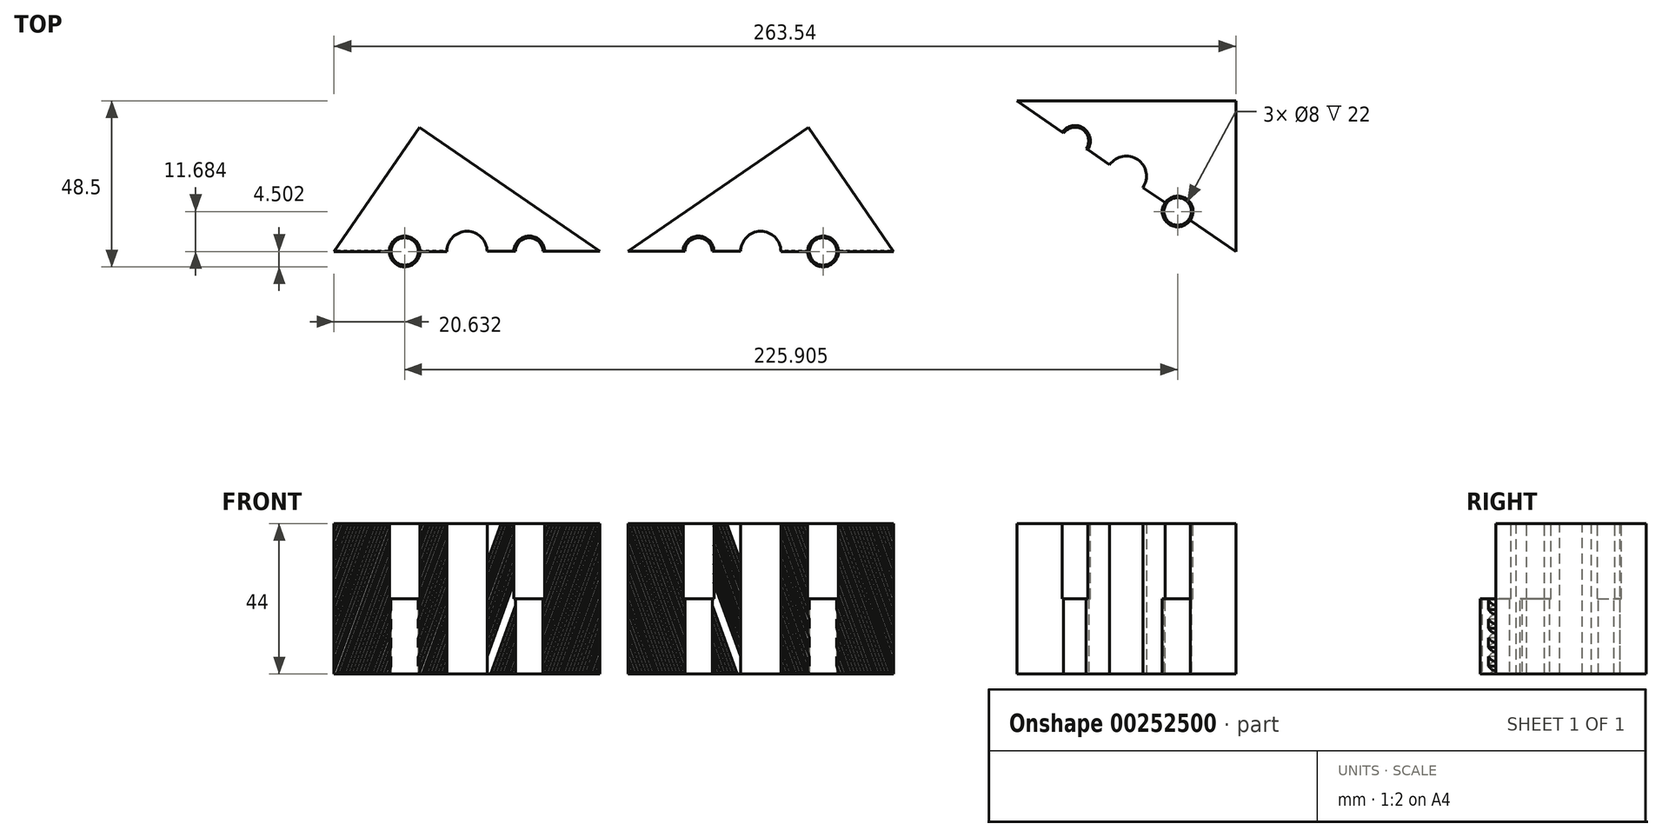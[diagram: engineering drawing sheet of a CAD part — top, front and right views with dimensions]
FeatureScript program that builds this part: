
annotation { "Feature Type Name" : "Feature", "Feature Type Description" : "" }
export const myFeature = defineFeature(function(context is Context, id is Id, definition is map)
    precondition{}
    {
        {
            var Q0;
            Q0=qCreatedBy(makeId("Top.planeOp"),FACE);
            var sketch = newSketch(context, id + "F0", { "sketchPlane" : qUnion([Q0])});
            skLineSegment(sketch, "E0.bottom", {"start": v(17.77, 54.78) * mm, "end": v(81.77, 54.78) * mm});
            skLineSegment(sketch, "E0.top", {"start": v(17.77, 10.78) * mm, "end": v(81.77, 10.78) * mm});
            skLineSegment(sketch, "E0.left", {"start": v(17.77, 54.78) * mm, "end": v(17.77, 10.78) * mm});
            skLineSegment(sketch, "E0.right", {"start": v(81.77, 54.78) * mm, "end": v(81.77, 10.78) * mm});
            skCircle(sketch, "E1", {"center": v(49.77, 32.78) * mm, "radius": 5.88 * mm});
            skPoint(sketch, "E1.centerSnap0", {"position": v(49.77, 54.78) * mm});
            skPoint(sketch, "E1.centerSnap1", {"position": v(17.77, 32.78) * mm});
            skCircle(sketch, "E2", {"center": v(34.77, 43.1) * mm, "radius": 4.5 * mm});
            skCircle(sketch, "E3", {"center": v(64.77, 22.47) * mm, "radius": 4.5 * mm});
            skLineSegment(sketch, "E4", {"start": v(34.77, -31.73) * mm, "end": v(64.77, -31.73) * mm, "construction": true});
            skPoint(sketch, "E5", {"position": v(49.77, -31.73) * mm});
            skLineSegment(sketch, "E6", {"start": v(17.77, 54.78) * mm, "end": v(81.77, 10.78) * mm, "construction": true});
            skCircle(sketch, "E7", {"center": v(34.77, 43.1) * mm, "radius": 4 * mm});
            skCircle(sketch, "E8", {"center": v(64.77, 22.47) * mm, "radius": 4 * mm});
            skSolve(sketch);
        }
        {
            var Q0;
            Q0=makeQuery(id+"F0.imprint","IMPRINT",FACE,{"disambiguationData":[TD([[makeQuery(id+"F0.imprint","IMPRINT",EDGE,{"derivedFrom":sQuery(id+"F0.wireOp",EDGE,"E0.bottom")}),-1.0]])]});
            var Q1;
            Q1=makeQuery(id+"F0.imprint","IMPRINT",FACE,{"disambiguationData":[TD([[makeQuery(id+"F0.imprint","IMPRINT",EDGE,{"derivedFrom":sQuery(id+"F0.wireOp",EDGE,"E3")}),1.0]])]});
            var Q2;
            Q2=makeQuery(id+"F0.imprint","IMPRINT",FACE,{"disambiguationData":[TD([[makeQuery(id+"F0.imprint","IMPRINT",EDGE,{"derivedFrom":sQuery(id+"F0.wireOp",EDGE,"E2")}),1.0]])]});
            extrude(context, id + "F1", {"entities" : qUnion([Q0, Q1, Q2]), "depth" : 44 * mm});
        }
        {
            var Q0;
            Q0=makeQuery(id+"F0.imprint","IMPRINT",FACE,{"disambiguationData":[TD([[makeQuery(id+"F0.imprint","IMPRINT",EDGE,{"derivedFrom":sQuery(id+"F0.wireOp",EDGE,"E1")}),1.0]])]});
            extrude(context, id + "F2", {"entities" : qUnion([Q0]), "operationType" : NewBodyOperationType.REMOVE, "depth" : 25 * mm});
        }
        {
            var Q0;
            Q0=makeQuery(id+"F1.opExtrude","CAP_FACE",FACE,{"disambiguationData":[OSD([sQuery(id+"F0.wireOp",EDGE,"E0.bottom"),sQuery(id+"F0.wireOp",EDGE,"E0.top"),sQuery(id+"F0.wireOp",EDGE,"E0.left"),sQuery(id+"F0.wireOp",EDGE,"E0.right"),sQuery(id+"F0.wireOp",EDGE,"E1"),sQuery(id+"F0.wireOp",EDGE,"E7"),sQuery(id+"F0.wireOp",EDGE,"E8")])],"isStart":false});
            var sketch = newSketch(context, id + "F3", { "sketchPlane" : qUnion([Q0])});
            skCircle(sketch, "E9", {"center": v(34.77, 43.1) * mm, "radius": 4 * mm});
            skCircle(sketch, "E10", {"center": v(64.77, 22.47) * mm, "radius": 4 * mm});
            skCircle(sketch, "E11", {"center": v(64.77, 22.47) * mm, "radius": 4.5 * mm});
            skCircle(sketch, "E12", {"center": v(34.77, 43.1) * mm, "radius": 4.5 * mm});
            skSolve(sketch);
        }
        {
            var Q0;
            Q0=makeQuery(id+"F3.imprint","IMPRINT",FACE,{"disambiguationData":[TD([[makeQuery(id+"F3.imprint","IMPRINT",EDGE,{"derivedFrom":sQuery(id+"F3.wireOp",EDGE,"E10")}),-1.0]])]});
            var Q1;
            Q1=makeQuery(id+"F3.imprint","IMPRINT",FACE,{"disambiguationData":[TD([[makeQuery(id+"F3.imprint","IMPRINT",EDGE,{"derivedFrom":sQuery(id+"F3.wireOp",EDGE,"E9")}),-1.0]])]});
            extrude(context, id + "F4", {"entities" : qUnion([Q0, Q1]), "operationType" : NewBodyOperationType.REMOVE, "oppositeDirection" : true, "depth" : 22 * mm});
        }
        {
            var Q0;
            Q0=makeQuery(id+"F1.opExtrude","CAP_FACE",FACE,{"disambiguationData":[OSD([sQuery(id+"F0.wireOp",EDGE,"E0.bottom"),sQuery(id+"F0.wireOp",EDGE,"E0.top"),sQuery(id+"F0.wireOp",EDGE,"E0.left"),sQuery(id+"F0.wireOp",EDGE,"E0.right"),sQuery(id+"F0.wireOp",EDGE,"E1"),sQuery(id+"F0.wireOp",EDGE,"E7"),sQuery(id+"F0.wireOp",EDGE,"E8")])],"isStart":false});
            var sketch = newSketch(context, id + "F5", { "sketchPlane" : qUnion([Q0])});
            skLineSegment(sketch, "E13", {"start": v(17.77, 54.78) * mm, "end": v(17.77, 10.78) * mm});
            skLineSegment(sketch, "E14", {"start": v(17.77, 10.78) * mm, "end": v(81.77, 10.78) * mm});
            skLineSegment(sketch, "E15", {"start": v(81.77, 10.78) * mm, "end": v(17.77, 54.78) * mm});
            skArc(sketch, "E16", {"start": v(31.06, 45.64) * mm, "mid": v(32.22, 39.38) * mm, "end": v(38.48, 40.54) * mm});
            skArc(sketch, "E17", {"start": v(31.47, 45.36) * mm, "mid": v(32.5, 39.8) * mm, "end": v(38.06, 40.83) * mm});
            skSolve(sketch);
        }
        {
            var Q0;
            {var subQ10=sQuery(id+"F5.wireOp",EDGE,"E13");Q0=makeQuery(id+"F5.imprint","IMPRINT",FACE,{"disambiguationData":[TD([[makeQuery(id+"F5.imprint","IMPRINT",EDGE,{"derivedFrom":subQ10}),1.0]])]});}
            var Q1;
            {var subQ0=sQuery(id+"F5.wireOp",EDGE,"E16");Q1=makeQuery(id+"F5.imprint","IMPRINT",FACE,{"disambiguationData":[TD([[makeQuery(id+"F5.imprint","IMPRINT",EDGE,{"derivedFrom":subQ0}),1.0]])]});}
            var Q2;
            {var subQ0=sQuery(id+"F5.wireOp",EDGE,"E15");var subQ1=makeQuery(id+"F4.boolean.opBoolean","COPY",EDGE,{"derivedFrom":makeQuery(id+"F4.opExtrude","CAP_EDGE",EDGE,{"disambiguationData":[OSD([sQuery(id+"F3.wireOp",EDGE,"E11")])],"isStart":true})});var subQ2=makeQuery(id+"F5.imprint","INTERSECT",VERTEX,{"disambiguationData":[OD(0.0)],"derivedFrom":[subQ1,subQ0]});Q2=makeQuery(id+"F5.imprint","IMPRINT",FACE,{"disambiguationData":[TD([[makeQuery(id+"F5.imprint","IMPRINT",EDGE,{"disambiguationData":[TD([[subQ2,-1.0]])],"derivedFrom":subQ0}),1.0]])]});}
            extrude(context, id + "F6", {"entities" : qUnion([Q0, Q1, Q2]), "operationType" : NewBodyOperationType.REMOVE, "oppositeDirection" : true, "depth" : 100 * mm});
        }
        {
            var Q0;
            Q0=makeQuery(id+"F1.opExtrude","SWEPT_BODY",BODY,{"disambiguationData":[OSD([sQuery(id+"F0.wireOp",EDGE,"E0.bottom"),sQuery(id+"F0.wireOp",EDGE,"E0.top"),sQuery(id+"F0.wireOp",EDGE,"E0.left"),sQuery(id+"F0.wireOp",EDGE,"E0.right"),sQuery(id+"F0.wireOp",EDGE,"E1"),sQuery(id+"F0.wireOp",EDGE,"E7"),sQuery(id+"F0.wireOp",EDGE,"E8")])]});
            transform(context, id + "F7", {"entities" : qUnion([Q0]), "transformType" : TransformType.TRANSLATION_3D, "dx" : 100 * mm, "dy" : 0 * mm, "dz" : 0 * mm, "makeCopy" : true});
        }
        {
            var Q0;
            Q0=makeQuery(id+"F1.opExtrude","SWEPT_BODY",BODY,{"disambiguationData":[OSD([sQuery(id+"F0.wireOp",EDGE,"E0.bottom"),sQuery(id+"F0.wireOp",EDGE,"E0.top"),sQuery(id+"F0.wireOp",EDGE,"E0.left"),sQuery(id+"F0.wireOp",EDGE,"E0.right"),sQuery(id+"F0.wireOp",EDGE,"E1"),sQuery(id+"F0.wireOp",EDGE,"E7"),sQuery(id+"F0.wireOp",EDGE,"E8")])]});
            var Q1;
            {var subQ0=sQuery(id+"F0.wireOp",EDGE,"E0.right");Q1=makeQuery(id+"F6.boolean.opBoolean","MERGE",EDGE,{"derivedFrom":[makeQuery(id+"F1.opExtrude","SWEPT_EDGE",EDGE,{"disambiguationData":[OSD([sQuery(id+"F0.wireOp",EDGE,"E0.top"),subQ0])]}),makeQuery(id+"F6.opExtrude","SWEPT_EDGE",EDGE,{"disambiguationData":[OSD([subQ0,sQuery(id+"F5.wireOp",EDGE,"E14"),sQuery(id+"F5.wireOp",EDGE,"E15")])]})]});}
            transform(context, id + "F8", {"entities" : qUnion([Q0]), "transformType" : TransformType.ROTATION, "transformAxis" : qUnion([Q1]), "angle" : 34.5 * degree, "oppositeDirection" : true, "makeCopy" : false});
        }
        {
            var Q0;
            Q0=qCreatedBy(makeId("Front.planeOp"),FACE);
            var sketch = newSketch(context, id + "F9", { "sketchPlane" : qUnion([Q0])});
            skLineSegment(sketch, "E18.bottom", {"start": v(-39.61, 0) * mm, "end": v(60.39, 0) * mm, "construction": true});
            skLineSegment(sketch, "E18.top", {"start": v(-39.61, 100) * mm, "end": v(60.39, 100) * mm, "construction": true});
            skLineSegment(sketch, "E18.left", {"start": v(-39.61, 0) * mm, "end": v(-39.61, 100) * mm, "construction": true});
            skLineSegment(sketch, "E18.right", {"start": v(60.39, 0) * mm, "end": v(60.39, 100) * mm, "construction": true});
            skLineSegment(sketch, "E19", {"start": v(-6.03, 0) * mm, "end": v(-39.61, 92.27) * mm});
            skLineSegment(sketch, "E20.1.0.0", {"start": v(-5.03, 0) * mm, "end": v(-38.61, 92.27) * mm});
            skLineSegment(sketch, "E20.2.0.0", {"start": v(-4.03, 0) * mm, "end": v(-37.61, 92.27) * mm});
            skLineSegment(sketch, "E20.3.0.0", {"start": v(-3.03, 0) * mm, "end": v(-36.61, 92.27) * mm});
            skLineSegment(sketch, "E20.4.0.0", {"start": v(-2.03, 0) * mm, "end": v(-35.61, 92.27) * mm});
            skLineSegment(sketch, "E20.5.0.0", {"start": v(-1.03, 0) * mm, "end": v(-34.61, 92.27) * mm});
            skLineSegment(sketch, "E20.6.0.0", {"start": v(-0.03, 0) * mm, "end": v(-33.61, 92.27) * mm});
            skLineSegment(sketch, "E20.7.0.0", {"start": v(0.97, 0) * mm, "end": v(-32.61, 92.27) * mm});
            skLineSegment(sketch, "E20.8.0.0", {"start": v(1.97, 0) * mm, "end": v(-31.61, 92.27) * mm});
            skLineSegment(sketch, "E20.9.0.0", {"start": v(2.97, 0) * mm, "end": v(-30.61, 92.27) * mm});
            skLineSegment(sketch, "E20.10.0.0", {"start": v(3.97, 0) * mm, "end": v(-29.61, 92.27) * mm});
            skLineSegment(sketch, "E20.11.0.0", {"start": v(4.97, 0) * mm, "end": v(-28.61, 92.27) * mm});
            skLineSegment(sketch, "E20.12.0.0", {"start": v(5.97, 0) * mm, "end": v(-27.61, 92.27) * mm});
            skLineSegment(sketch, "E20.13.0.0", {"start": v(6.97, 0) * mm, "end": v(-26.61, 92.27) * mm});
            skLineSegment(sketch, "E20.14.0.0", {"start": v(7.97, 0) * mm, "end": v(-25.61, 92.27) * mm});
            skLineSegment(sketch, "E20.15.0.0", {"start": v(8.97, 0) * mm, "end": v(-24.61, 92.27) * mm});
            skLineSegment(sketch, "E20.16.0.0", {"start": v(9.97, 0) * mm, "end": v(-23.61, 92.27) * mm});
            skLineSegment(sketch, "E20.17.0.0", {"start": v(10.97, 0) * mm, "end": v(-22.61, 92.27) * mm});
            skLineSegment(sketch, "E20.18.0.0", {"start": v(11.97, 0) * mm, "end": v(-21.61, 92.27) * mm});
            skLineSegment(sketch, "E20.19.0.0", {"start": v(12.97, 0) * mm, "end": v(-20.61, 92.27) * mm});
            skLineSegment(sketch, "E20.20.0.0", {"start": v(13.97, 0) * mm, "end": v(-19.61, 92.27) * mm});
            skLineSegment(sketch, "E20.21.0.0", {"start": v(14.97, 0) * mm, "end": v(-18.61, 92.27) * mm});
            skLineSegment(sketch, "E20.22.0.0", {"start": v(15.97, 0) * mm, "end": v(-17.61, 92.27) * mm});
            skLineSegment(sketch, "E20.23.0.0", {"start": v(16.97, 0) * mm, "end": v(-16.61, 92.27) * mm});
            skLineSegment(sketch, "E20.24.0.0", {"start": v(17.97, 0) * mm, "end": v(-15.61, 92.27) * mm});
            skLineSegment(sketch, "E20.25.0.0", {"start": v(18.97, 0) * mm, "end": v(-14.61, 92.27) * mm});
            skLineSegment(sketch, "E20.26.0.0", {"start": v(19.97, 0) * mm, "end": v(-13.61, 92.27) * mm});
            skLineSegment(sketch, "E20.27.0.0", {"start": v(20.97, 0) * mm, "end": v(-12.61, 92.27) * mm});
            skLineSegment(sketch, "E20.28.0.0", {"start": v(21.97, 0) * mm, "end": v(-11.61, 92.27) * mm});
            skLineSegment(sketch, "E20.29.0.0", {"start": v(22.97, 0) * mm, "end": v(-10.61, 92.27) * mm});
            skLineSegment(sketch, "E20.30.0.0", {"start": v(23.97, 0) * mm, "end": v(-9.61, 92.27) * mm});
            skLineSegment(sketch, "E20.31.0.0", {"start": v(24.97, 0) * mm, "end": v(-8.61, 92.27) * mm});
            skLineSegment(sketch, "E20.32.0.0", {"start": v(25.97, 0) * mm, "end": v(-7.61, 92.27) * mm});
            skLineSegment(sketch, "E20.33.0.0", {"start": v(26.97, 0) * mm, "end": v(-6.61, 92.27) * mm});
            skLineSegment(sketch, "E20.34.0.0", {"start": v(27.97, 0) * mm, "end": v(-5.61, 92.27) * mm});
            skLineSegment(sketch, "E20.35.0.0", {"start": v(28.97, 0) * mm, "end": v(-4.61, 92.27) * mm});
            skLineSegment(sketch, "E20.36.0.0", {"start": v(29.97, 0) * mm, "end": v(-3.61, 92.27) * mm});
            skLineSegment(sketch, "E20.37.0.0", {"start": v(30.97, 0) * mm, "end": v(-2.61, 92.27) * mm});
            skLineSegment(sketch, "E20.38.0.0", {"start": v(31.97, 0) * mm, "end": v(-1.61, 92.27) * mm});
            skLineSegment(sketch, "E20.39.0.0", {"start": v(32.97, 0) * mm, "end": v(-0.61, 92.27) * mm});
            skLineSegment(sketch, "E20.40.0.0", {"start": v(33.97, 0) * mm, "end": v(0.39, 92.27) * mm});
            skLineSegment(sketch, "E20.41.0.0", {"start": v(34.97, 0) * mm, "end": v(1.39, 92.27) * mm});
            skLineSegment(sketch, "E20.42.0.0", {"start": v(35.97, 0) * mm, "end": v(2.39, 92.27) * mm});
            skLineSegment(sketch, "E20.43.0.0", {"start": v(36.97, 0) * mm, "end": v(3.39, 92.27) * mm});
            skLineSegment(sketch, "E20.44.0.0", {"start": v(37.97, 0) * mm, "end": v(4.39, 92.27) * mm});
            skLineSegment(sketch, "E20.45.0.0", {"start": v(38.97, 0) * mm, "end": v(5.39, 92.27) * mm});
            skLineSegment(sketch, "E20.46.0.0", {"start": v(39.97, 0) * mm, "end": v(6.39, 92.27) * mm});
            skLineSegment(sketch, "E20.47.0.0", {"start": v(40.97, 0) * mm, "end": v(7.39, 92.27) * mm});
            skLineSegment(sketch, "E20.48.0.0", {"start": v(41.97, 0) * mm, "end": v(8.39, 92.27) * mm});
            skLineSegment(sketch, "E20.49.0.0", {"start": v(42.97, 0) * mm, "end": v(9.39, 92.27) * mm});
            skLineSegment(sketch, "E20.50.0.0", {"start": v(43.97, 0) * mm, "end": v(10.39, 92.27) * mm});
            skLineSegment(sketch, "E20.51.0.0", {"start": v(44.97, 0) * mm, "end": v(11.39, 92.27) * mm});
            skLineSegment(sketch, "E20.52.0.0", {"start": v(45.97, 0) * mm, "end": v(12.39, 92.27) * mm});
            skLineSegment(sketch, "E20.53.0.0", {"start": v(46.97, 0) * mm, "end": v(13.39, 92.27) * mm});
            skLineSegment(sketch, "E20.54.0.0", {"start": v(47.97, 0) * mm, "end": v(14.39, 92.27) * mm});
            skLineSegment(sketch, "E20.55.0.0", {"start": v(48.97, 0) * mm, "end": v(15.39, 92.27) * mm});
            skLineSegment(sketch, "E20.56.0.0", {"start": v(49.97, 0) * mm, "end": v(16.39, 92.27) * mm});
            skLineSegment(sketch, "E20.57.0.0", {"start": v(50.97, 0) * mm, "end": v(17.39, 92.27) * mm});
            skLineSegment(sketch, "E20.58.0.0", {"start": v(51.97, 0) * mm, "end": v(18.39, 92.27) * mm});
            skLineSegment(sketch, "E20.59.0.0", {"start": v(52.97, 0) * mm, "end": v(19.39, 92.27) * mm});
            skLineSegment(sketch, "E20.60.0.0", {"start": v(53.97, 0) * mm, "end": v(20.39, 92.27) * mm});
            skLineSegment(sketch, "E20.61.0.0", {"start": v(54.97, 0) * mm, "end": v(21.39, 92.27) * mm});
            skLineSegment(sketch, "E20.62.0.0", {"start": v(55.97, 0) * mm, "end": v(22.39, 92.27) * mm});
            skLineSegment(sketch, "E20.63.0.0", {"start": v(56.97, 0) * mm, "end": v(23.39, 92.27) * mm});
            skLineSegment(sketch, "E20.64.0.0", {"start": v(57.97, 0) * mm, "end": v(24.39, 92.27) * mm});
            skLineSegment(sketch, "E20.65.0.0", {"start": v(58.97, 0) * mm, "end": v(25.39, 92.27) * mm});
            skLineSegment(sketch, "E20.66.0.0", {"start": v(59.97, 0) * mm, "end": v(26.39, 92.27) * mm});
            skLineSegment(sketch, "E20.67.0.0", {"start": v(60.97, 0) * mm, "end": v(27.39, 92.27) * mm});
            skLineSegment(sketch, "E20.68.0.0", {"start": v(61.97, 0) * mm, "end": v(28.39, 92.27) * mm});
            skLineSegment(sketch, "E20.69.0.0", {"start": v(62.97, 0) * mm, "end": v(29.39, 92.27) * mm});
            skLineSegment(sketch, "E20.70.0.0", {"start": v(63.97, 0) * mm, "end": v(30.39, 92.27) * mm});
            skLineSegment(sketch, "E20.71.0.0", {"start": v(64.97, 0) * mm, "end": v(31.39, 92.27) * mm});
            skLineSegment(sketch, "E20.72.0.0", {"start": v(65.97, 0) * mm, "end": v(32.39, 92.27) * mm});
            skLineSegment(sketch, "E20.73.0.0", {"start": v(66.97, 0) * mm, "end": v(33.39, 92.27) * mm});
            skLineSegment(sketch, "E20.74.0.0", {"start": v(67.97, 0) * mm, "end": v(34.39, 92.27) * mm});
            skLineSegment(sketch, "E20.75.0.0", {"start": v(68.97, 0) * mm, "end": v(35.39, 92.27) * mm});
            skLineSegment(sketch, "E20.76.0.0", {"start": v(69.97, 0) * mm, "end": v(36.39, 92.27) * mm});
            skLineSegment(sketch, "E20.77.0.0", {"start": v(70.97, 0) * mm, "end": v(37.39, 92.27) * mm});
            skLineSegment(sketch, "E20.78.0.0", {"start": v(71.97, 0) * mm, "end": v(38.39, 92.27) * mm});
            skLineSegment(sketch, "E20.79.0.0", {"start": v(72.97, 0) * mm, "end": v(39.39, 92.27) * mm});
            skLineSegment(sketch, "E20.80.0.0", {"start": v(73.97, 0) * mm, "end": v(40.39, 92.27) * mm});
            skLineSegment(sketch, "E20.81.0.0", {"start": v(74.97, 0) * mm, "end": v(41.39, 92.27) * mm});
            skLineSegment(sketch, "E20.82.0.0", {"start": v(75.97, 0) * mm, "end": v(42.39, 92.27) * mm});
            skLineSegment(sketch, "E20.83.0.0", {"start": v(76.97, 0) * mm, "end": v(43.39, 92.27) * mm});
            skLineSegment(sketch, "E20.84.0.0", {"start": v(77.97, 0) * mm, "end": v(44.39, 92.27) * mm});
            skLineSegment(sketch, "E20.85.0.0", {"start": v(78.97, 0) * mm, "end": v(45.39, 92.27) * mm});
            skLineSegment(sketch, "E20.86.0.0", {"start": v(79.97, 0) * mm, "end": v(46.39, 92.27) * mm});
            skLineSegment(sketch, "E20.87.0.0", {"start": v(80.97, 0) * mm, "end": v(47.39, 92.27) * mm});
            skLineSegment(sketch, "E20.88.0.0", {"start": v(81.97, 0) * mm, "end": v(48.39, 92.27) * mm});
            skLineSegment(sketch, "E20.89.0.0", {"start": v(82.97, 0) * mm, "end": v(49.39, 92.27) * mm});
            skLineSegment(sketch, "E20.90.0.0", {"start": v(83.97, 0) * mm, "end": v(50.39, 92.27) * mm});
            skLineSegment(sketch, "E20.91.0.0", {"start": v(84.97, 0) * mm, "end": v(51.39, 92.27) * mm});
            skLineSegment(sketch, "E20.92.0.0", {"start": v(85.97, 0) * mm, "end": v(52.39, 92.27) * mm});
            skLineSegment(sketch, "E20.93.0.0", {"start": v(86.97, 0) * mm, "end": v(53.39, 92.27) * mm});
            skLineSegment(sketch, "E20.94.0.0", {"start": v(87.97, 0) * mm, "end": v(54.39, 92.27) * mm});
            skLineSegment(sketch, "E20.95.0.0", {"start": v(88.97, 0) * mm, "end": v(55.39, 92.27) * mm});
            skLineSegment(sketch, "E20.96.0.0", {"start": v(89.97, 0) * mm, "end": v(56.39, 92.27) * mm});
            skLineSegment(sketch, "E20.97.0.0", {"start": v(90.97, 0) * mm, "end": v(57.39, 92.27) * mm});
            skLineSegment(sketch, "E20.98.0.0", {"start": v(91.97, 0) * mm, "end": v(58.39, 92.27) * mm});
            skLineSegment(sketch, "E20.99.0.0", {"start": v(92.97, 0) * mm, "end": v(59.39, 92.27) * mm});
            skLineSegment(sketch, "E20.direction1", {"start": v(-6.03, 0) * mm, "end": v(-5.03, 0) * mm, "construction": true});
            skLineSegment(sketch, "E21.top", {"start": v(37.77, 0) * mm, "end": v(44.67, 0) * mm});
            skLineSegment(sketch, "E22", {"start": v(48.67, 0) * mm, "end": v(56.77, 0) * mm});
            skLineSegment(sketch, "E23.MirrorCS", {"start": v(139.15, 0) * mm, "end": v(39.15, 0) * mm, "construction": true});
            skLineSegment(sketch, "E24.bottom", {"start": v(20.23, 44) * mm, "end": v(29.23, 44) * mm});
            skLineSegment(sketch, "E24.top", {"start": v(20.23, 22) * mm, "end": v(29.23, 22) * mm});
            skLineSegment(sketch, "E24.left", {"start": v(20.23, 44) * mm, "end": v(20.23, 22) * mm});
            skLineSegment(sketch, "E24.right", {"start": v(29.23, 44) * mm, "end": v(29.23, 22) * mm});
            skLineSegment(sketch, "E25.bottom", {"start": v(20.73, 22) * mm, "end": v(28.73, 22) * mm});
            skLineSegment(sketch, "E25.top", {"start": v(20.73, 0) * mm, "end": v(28.73, 0) * mm});
            skLineSegment(sketch, "E25.left", {"start": v(20.73, 22) * mm, "end": v(20.73, 0) * mm});
            skLineSegment(sketch, "E25.right", {"start": v(28.73, 22) * mm, "end": v(28.73, 0) * mm});
            skLineSegment(sketch, "E26", {"start": v(4.1, -46.77) * mm, "end": v(81.77, -46.77) * mm, "construction": true});
            skPoint(sketch, "E27", {"position": v(4.1, 1.38) * mm});
            skPoint(sketch, "E28", {"position": v(42.93, -46.77) * mm});
            skLineSegment(sketch, "E29", {"start": v(20.73, -2) * mm, "end": v(28.73, -2) * mm, "construction": true});
            skLineSegment(sketch, "E30.bottom", {"start": v(56.64, 44) * mm, "end": v(65.64, 44) * mm});
            skLineSegment(sketch, "E30.top", {"start": v(56.64, 22) * mm, "end": v(65.64, 22) * mm});
            skLineSegment(sketch, "E30.left", {"start": v(56.64, 44) * mm, "end": v(56.64, 22) * mm});
            skLineSegment(sketch, "E30.right", {"start": v(65.64, 44) * mm, "end": v(65.64, 22) * mm});
            skLineSegment(sketch, "E31.bottom", {"start": v(57.14, 22) * mm, "end": v(65.14, 22) * mm});
            skLineSegment(sketch, "E31.top", {"start": v(57.14, 0) * mm, "end": v(65.14, 0) * mm});
            skLineSegment(sketch, "E31.left", {"start": v(57.14, 22) * mm, "end": v(57.14, 0) * mm});
            skLineSegment(sketch, "E31.right", {"start": v(65.14, 22) * mm, "end": v(65.14, 0) * mm});
            skLineSegment(sketch, "E32.bottom", {"start": v(4.1, 44) * mm, "end": v(20.23, 44) * mm});
            skLineSegment(sketch, "E32.left", {"start": v(4.1, 44) * mm, "end": v(4.1, 22) * mm});
            skLineSegment(sketch, "E33.top", {"start": v(4.1, 0) * mm, "end": v(20.73, 0) * mm});
            skLineSegment(sketch, "E33.left", {"start": v(4.1, 22) * mm, "end": v(4.1, 0) * mm});
            skLineSegment(sketch, "E34.trimOffspring", {"start": v(20.23, 22) * mm, "end": v(20.73, 22) * mm});
            skLineSegment(sketch, "E35.bottom", {"start": v(29.23, 44) * mm, "end": v(37.06, 44) * mm});
            skLineSegment(sketch, "E35.right", {"start": v(37.06, 44) * mm, "end": v(37.06, 22) * mm});
            skLineSegment(sketch, "E36.bottom", {"start": v(28.73, 22) * mm, "end": v(28.97, 22) * mm});
            skLineSegment(sketch, "E36.top", {"start": v(28.73, 0) * mm, "end": v(37.06, 0) * mm});
            skLineSegment(sketch, "E36.right", {"start": v(37.06, 22) * mm, "end": v(37.06, 0) * mm});
            skLineSegment(sketch, "E37.trimOffspring", {"start": v(36.97, 22) * mm, "end": v(37.06, 22) * mm});
            skLineSegment(sketch, "E38.top", {"start": v(57.14, 0) * mm, "end": v(48.8, 0) * mm});
            skLineSegment(sketch, "E38.right", {"start": v(48.8, 22) * mm, "end": v(48.8, 0) * mm});
            skLineSegment(sketch, "E39.top", {"start": v(56.64, 44) * mm, "end": v(48.8, 44) * mm});
            skLineSegment(sketch, "E39.left", {"start": v(56.64, 22) * mm, "end": v(56.64, 44) * mm});
            skLineSegment(sketch, "E39.right", {"start": v(48.8, 22) * mm, "end": v(48.8, 44) * mm});
            skLineSegment(sketch, "E40.1.0.0", {"start": v(93.97, 0) * mm, "end": v(60.39, 92.27) * mm});
            skLineSegment(sketch, "E40.2.0.0", {"start": v(94.97, 0) * mm, "end": v(61.39, 92.27) * mm});
            skLineSegment(sketch, "E40.3.0.0", {"start": v(95.97, 0) * mm, "end": v(62.39, 92.27) * mm});
            skLineSegment(sketch, "E40.4.0.0", {"start": v(96.97, 0) * mm, "end": v(63.39, 92.27) * mm});
            skLineSegment(sketch, "E40.5.0.0", {"start": v(97.97, 0) * mm, "end": v(64.39, 92.27) * mm});
            skLineSegment(sketch, "E40.6.0.0", {"start": v(98.97, 0) * mm, "end": v(65.39, 92.27) * mm});
            skLineSegment(sketch, "E40.7.0.0", {"start": v(99.97, 0) * mm, "end": v(66.39, 92.27) * mm});
            skLineSegment(sketch, "E40.8.0.0", {"start": v(100.97, 0) * mm, "end": v(67.39, 92.27) * mm});
            skLineSegment(sketch, "E40.9.0.0", {"start": v(101.97, 0) * mm, "end": v(68.39, 92.27) * mm});
            skLineSegment(sketch, "E40.direction1", {"start": v(92.97, 0) * mm, "end": v(93.97, 0) * mm, "construction": true});
            skLineSegment(sketch, "E41.bottom", {"start": v(65.64, 44) * mm, "end": v(81.77, 44) * mm});
            skLineSegment(sketch, "E41.right", {"start": v(81.77, 44) * mm, "end": v(81.77, 22) * mm});
            skLineSegment(sketch, "E42.bottom", {"start": v(65.14, 0) * mm, "end": v(81.77, 0) * mm});
            skLineSegment(sketch, "E42.left", {"start": v(65.14, 0) * mm, "end": v(65.14, 22) * mm});
            skLineSegment(sketch, "E42.right", {"start": v(81.77, 0) * mm, "end": v(81.77, 22) * mm});
            skLineSegment(sketch, "E43", {"start": v(4.2, 0) * mm, "end": v(4.2, 44) * mm});
            skLineSegment(sketch, "E44", {"start": v(42.93, -44.84) * mm, "end": v(42.93, -27.61) * mm, "construction": true});
            skLineSegment(sketch, "E45.MirrorCS", {"start": v(81.67, 0) * mm, "end": v(81.67, 44) * mm});
            skSolve(sketch);
        }
        {
            var Q0;
            Q0=qCreatedBy(makeId("Top.planeOp"),FACE);
            var sketch = newSketch(context, id + "F10", { "sketchPlane" : qUnion([Q0])});
            skLineSegment(sketch, "E46", {"start": v(-18.8, 10.9) * mm, "end": v(-18.7, 10.9) * mm, "construction": true});
            skSolve(sketch);
        }
        {
            var Q0;
            {var subQ0=sQuery(id+"F9.wireOp",EDGE,"E33.top");var subQ1=sQuery(id+"F9.wireOp",EDGE,"E20.13.0.0");var subQ2=makeQuery(id+"F9.imprint","INTERSECT",VERTEX,{"derivedFrom":[subQ1,subQ0]});Q0=makeQuery(id+"F9.imprint","IMPRINT",FACE,{"disambiguationData":[TD([[makeQuery(id+"F9.imprint","IMPRINT",EDGE,{"disambiguationData":[TD([[subQ2,-1.0]])],"derivedFrom":subQ1}),-1.0]])]});}
            var Q1;
            {var subQ0=sQuery(id+"F9.wireOp",EDGE,"E33.top");var subQ1=sQuery(id+"F9.wireOp",EDGE,"E20.15.0.0");var subQ2=makeQuery(id+"F9.imprint","INTERSECT",VERTEX,{"derivedFrom":[subQ1,subQ0]});Q1=makeQuery(id+"F9.imprint","IMPRINT",FACE,{"disambiguationData":[TD([[makeQuery(id+"F9.imprint","IMPRINT",EDGE,{"disambiguationData":[TD([[subQ2,-1.0]])],"derivedFrom":subQ1}),-1.0]])]});}
            var Q2;
            {var subQ0=sQuery(id+"F9.wireOp",EDGE,"E33.top");var subQ1=sQuery(id+"F9.wireOp",EDGE,"E20.17.0.0");var subQ2=makeQuery(id+"F9.imprint","INTERSECT",VERTEX,{"derivedFrom":[subQ1,subQ0]});Q2=makeQuery(id+"F9.imprint","IMPRINT",FACE,{"disambiguationData":[TD([[makeQuery(id+"F9.imprint","IMPRINT",EDGE,{"disambiguationData":[TD([[subQ2,-1.0]])],"derivedFrom":subQ1}),-1.0]])]});}
            var Q3;
            {var subQ0=sQuery(id+"F9.wireOp",EDGE,"E33.top");var subQ1=sQuery(id+"F9.wireOp",EDGE,"E20.19.0.0");var subQ2=makeQuery(id+"F9.imprint","INTERSECT",VERTEX,{"derivedFrom":[subQ1,subQ0]});Q3=makeQuery(id+"F9.imprint","IMPRINT",FACE,{"disambiguationData":[TD([[makeQuery(id+"F9.imprint","IMPRINT",EDGE,{"disambiguationData":[TD([[subQ2,-1.0]])],"derivedFrom":subQ1}),-1.0]])]});}
            var Q4;
            {var subQ0=sQuery(id+"F9.wireOp",EDGE,"E33.top");var subQ1=sQuery(id+"F9.wireOp",EDGE,"E20.21.0.0");var subQ2=makeQuery(id+"F9.imprint","INTERSECT",VERTEX,{"derivedFrom":[subQ1,subQ0]});Q4=makeQuery(id+"F9.imprint","IMPRINT",FACE,{"disambiguationData":[TD([[makeQuery(id+"F9.imprint","IMPRINT",EDGE,{"disambiguationData":[TD([[subQ2,-1.0]])],"derivedFrom":subQ1}),-1.0]])]});}
            var Q5;
            {var subQ0=sQuery(id+"F9.wireOp",EDGE,"E33.top");var subQ1=sQuery(id+"F9.wireOp",EDGE,"E20.23.0.0");var subQ2=makeQuery(id+"F9.imprint","INTERSECT",VERTEX,{"derivedFrom":[subQ1,subQ0]});Q5=makeQuery(id+"F9.imprint","IMPRINT",FACE,{"disambiguationData":[TD([[makeQuery(id+"F9.imprint","IMPRINT",EDGE,{"disambiguationData":[TD([[subQ2,-1.0]])],"derivedFrom":subQ1}),-1.0]])]});}
            var Q6;
            {var subQ0=sQuery(id+"F9.wireOp",EDGE,"E33.top");var subQ1=sQuery(id+"F9.wireOp",EDGE,"E20.25.0.0");var subQ2=makeQuery(id+"F9.imprint","INTERSECT",VERTEX,{"derivedFrom":[subQ1,subQ0]});Q6=makeQuery(id+"F9.imprint","IMPRINT",FACE,{"disambiguationData":[TD([[makeQuery(id+"F9.imprint","IMPRINT",EDGE,{"disambiguationData":[TD([[subQ2,-1.0]])],"derivedFrom":subQ1}),-1.0]])]});}
            var Q7;
            {var subQ0=sQuery(id+"F9.wireOp",EDGE,"E32.bottom");var subQ1=sQuery(id+"F9.wireOp",EDGE,"E20.29.0.0");var subQ2=makeQuery(id+"F9.imprint","INTERSECT",VERTEX,{"derivedFrom":[subQ1,subQ0]});Q7=makeQuery(id+"F9.imprint","IMPRINT",FACE,{"disambiguationData":[TD([[makeQuery(id+"F9.imprint","IMPRINT",EDGE,{"disambiguationData":[TD([[subQ2,1.0]])],"derivedFrom":subQ1}),-1.0]])]});}
            var Q8;
            {var subQ0=sQuery(id+"F9.wireOp",EDGE,"E32.bottom");var subQ1=sQuery(id+"F9.wireOp",EDGE,"E20.31.0.0");var subQ2=makeQuery(id+"F9.imprint","INTERSECT",VERTEX,{"derivedFrom":[subQ1,subQ0]});Q8=makeQuery(id+"F9.imprint","IMPRINT",FACE,{"disambiguationData":[TD([[makeQuery(id+"F9.imprint","IMPRINT",EDGE,{"disambiguationData":[TD([[subQ2,1.0]])],"derivedFrom":subQ1}),-1.0]])]});}
            var Q9;
            {var subQ0=sQuery(id+"F9.wireOp",EDGE,"E32.bottom");var subQ1=sQuery(id+"F9.wireOp",EDGE,"E20.33.0.0");var subQ2=makeQuery(id+"F9.imprint","INTERSECT",VERTEX,{"derivedFrom":[subQ1,subQ0]});Q9=makeQuery(id+"F9.imprint","IMPRINT",FACE,{"disambiguationData":[TD([[makeQuery(id+"F9.imprint","IMPRINT",EDGE,{"disambiguationData":[TD([[subQ2,1.0]])],"derivedFrom":subQ1}),-1.0]])]});}
            var Q10;
            {var subQ0=sQuery(id+"F9.wireOp",EDGE,"E32.bottom");var subQ1=sQuery(id+"F9.wireOp",EDGE,"E20.35.0.0");var subQ2=makeQuery(id+"F9.imprint","INTERSECT",VERTEX,{"derivedFrom":[subQ1,subQ0]});Q10=makeQuery(id+"F9.imprint","IMPRINT",FACE,{"disambiguationData":[TD([[makeQuery(id+"F9.imprint","IMPRINT",EDGE,{"disambiguationData":[TD([[subQ2,1.0]])],"derivedFrom":subQ1}),-1.0]])]});}
            var Q11;
            {var subQ0=sQuery(id+"F9.wireOp",EDGE,"E32.bottom");var subQ1=sQuery(id+"F9.wireOp",EDGE,"E20.37.0.0");var subQ2=makeQuery(id+"F9.imprint","INTERSECT",VERTEX,{"derivedFrom":[subQ1,subQ0]});Q11=makeQuery(id+"F9.imprint","IMPRINT",FACE,{"disambiguationData":[TD([[makeQuery(id+"F9.imprint","IMPRINT",EDGE,{"disambiguationData":[TD([[subQ2,1.0]])],"derivedFrom":subQ1}),-1.0]])]});}
            var Q12;
            {var subQ0=sQuery(id+"F9.wireOp",EDGE,"E32.bottom");var subQ1=sQuery(id+"F9.wireOp",EDGE,"E20.39.0.0");var subQ2=makeQuery(id+"F9.imprint","INTERSECT",VERTEX,{"derivedFrom":[subQ1,subQ0]});Q12=makeQuery(id+"F9.imprint","IMPRINT",FACE,{"disambiguationData":[TD([[makeQuery(id+"F9.imprint","IMPRINT",EDGE,{"disambiguationData":[TD([[subQ2,1.0]])],"derivedFrom":subQ1}),-1.0]])]});}
            var Q13;
            {var subQ0=sQuery(id+"F9.wireOp",EDGE,"E32.bottom");var subQ1=sQuery(id+"F9.wireOp",EDGE,"E20.41.0.0");var subQ2=makeQuery(id+"F9.imprint","INTERSECT",VERTEX,{"derivedFrom":[subQ1,subQ0]});Q13=makeQuery(id+"F9.imprint","IMPRINT",FACE,{"disambiguationData":[TD([[makeQuery(id+"F9.imprint","IMPRINT",EDGE,{"disambiguationData":[TD([[subQ2,1.0]])],"derivedFrom":subQ1}),-1.0]])]});}
            var Q14;
            {var subQ0=sQuery(id+"F9.wireOp",EDGE,"E36.top");var subQ1=sQuery(id+"F9.wireOp",EDGE,"E20.35.0.0");var subQ2=makeQuery(id+"F9.imprint","INTERSECT",VERTEX,{"derivedFrom":[subQ1,subQ0]});Q14=makeQuery(id+"F9.imprint","IMPRINT",FACE,{"disambiguationData":[TD([[makeQuery(id+"F9.imprint","IMPRINT",EDGE,{"disambiguationData":[TD([[subQ2,-1.0]])],"derivedFrom":subQ1}),-1.0]])]});}
            var Q15;
            {var subQ0=sQuery(id+"F9.wireOp",EDGE,"E36.top");var subQ1=sQuery(id+"F9.wireOp",EDGE,"E20.37.0.0");var subQ2=makeQuery(id+"F9.imprint","INTERSECT",VERTEX,{"derivedFrom":[subQ1,subQ0]});Q15=makeQuery(id+"F9.imprint","IMPRINT",FACE,{"disambiguationData":[TD([[makeQuery(id+"F9.imprint","IMPRINT",EDGE,{"disambiguationData":[TD([[subQ2,-1.0]])],"derivedFrom":subQ1}),-1.0]])]});}
            var Q16;
            {var subQ0=sQuery(id+"F9.wireOp",EDGE,"E36.top");var subQ1=sQuery(id+"F9.wireOp",EDGE,"E20.39.0.0");var subQ2=makeQuery(id+"F9.imprint","INTERSECT",VERTEX,{"derivedFrom":[subQ1,subQ0]});Q16=makeQuery(id+"F9.imprint","IMPRINT",FACE,{"disambiguationData":[TD([[makeQuery(id+"F9.imprint","IMPRINT",EDGE,{"disambiguationData":[TD([[subQ2,-1.0]])],"derivedFrom":subQ1}),-1.0]])]});}
            var Q17;
            {var subQ0=sQuery(id+"F9.wireOp",EDGE,"E36.top");var subQ1=sQuery(id+"F9.wireOp",EDGE,"E20.41.0.0");var subQ2=makeQuery(id+"F9.imprint","INTERSECT",VERTEX,{"derivedFrom":[subQ1,subQ0]});Q17=makeQuery(id+"F9.imprint","IMPRINT",FACE,{"disambiguationData":[TD([[makeQuery(id+"F9.imprint","IMPRINT",EDGE,{"disambiguationData":[TD([[subQ2,-1.0]])],"derivedFrom":subQ1}),-1.0]])]});}
            var Q18;
            {var subQ0=sQuery(id+"F9.wireOp",EDGE,"E24.top");Q18=makeQuery(id+"F9.imprint","IMPRINT",FACE,{"disambiguationData":[TD([[makeQuery(id+"F9.imprint","IMPRINT",EDGE,{"derivedFrom":subQ0}),-1.0]])]});}
            var Q19;
            {var subQ0=sQuery(id+"F9.wireOp",EDGE,"E36.right");var subQ1=sQuery(id+"F9.wireOp",EDGE,"E20.45.0.0");var subQ2=makeQuery(id+"F9.imprint","INTERSECT",VERTEX,{"derivedFrom":[subQ1,subQ0]});Q19=makeQuery(id+"F9.imprint","IMPRINT",FACE,{"disambiguationData":[TD([[makeQuery(id+"F9.imprint","IMPRINT",EDGE,{"disambiguationData":[TD([[subQ2,-1.0]])],"derivedFrom":subQ1}),-1.0]])]});}
            var Q20;
            {var subQ0=sQuery(id+"F9.wireOp",EDGE,"E36.right");var subQ1=sQuery(id+"F9.wireOp",EDGE,"E20.47.0.0");var subQ2=makeQuery(id+"F9.imprint","INTERSECT",VERTEX,{"derivedFrom":[subQ1,subQ0]});Q20=makeQuery(id+"F9.imprint","IMPRINT",FACE,{"disambiguationData":[TD([[makeQuery(id+"F9.imprint","IMPRINT",EDGE,{"disambiguationData":[TD([[subQ2,-1.0]])],"derivedFrom":subQ1}),-1.0]])]});}
            var Q21;
            {var subQ0=sQuery(id+"F9.wireOp",EDGE,"E36.right");var subQ1=sQuery(id+"F9.wireOp",EDGE,"E20.49.0.0");var subQ2=makeQuery(id+"F9.imprint","INTERSECT",VERTEX,{"derivedFrom":[subQ1,subQ0]});Q21=makeQuery(id+"F9.imprint","IMPRINT",FACE,{"disambiguationData":[TD([[makeQuery(id+"F9.imprint","IMPRINT",EDGE,{"disambiguationData":[TD([[subQ2,-1.0]])],"derivedFrom":subQ1}),-1.0]])]});}
            var Q22;
            {var subQ9=sQuery(id+"F9.wireOp",EDGE,"E37.trimOffspring");Q22=makeQuery(id+"F9.imprint","IMPRINT",FACE,{"disambiguationData":[TD([[makeQuery(id+"F9.imprint","IMPRINT",EDGE,{"derivedFrom":subQ9}),1.0]])]});}
            var Q23;
            {var subQ0=sQuery(id+"F9.wireOp",EDGE,"E35.bottom");var subQ1=sQuery(id+"F9.wireOp",EDGE,"E20.53.0.0");var subQ2=makeQuery(id+"F9.imprint","INTERSECT",VERTEX,{"derivedFrom":[subQ1,subQ0]});Q23=makeQuery(id+"F9.imprint","IMPRINT",FACE,{"disambiguationData":[TD([[makeQuery(id+"F9.imprint","IMPRINT",EDGE,{"disambiguationData":[TD([[subQ2,1.0]])],"derivedFrom":subQ1}),-1.0]])]});}
            var Q24;
            {var subQ0=sQuery(id+"F9.wireOp",EDGE,"E35.bottom");var subQ1=sQuery(id+"F9.wireOp",EDGE,"E20.55.0.0");var subQ2=makeQuery(id+"F9.imprint","INTERSECT",VERTEX,{"derivedFrom":[subQ1,subQ0]});Q24=makeQuery(id+"F9.imprint","IMPRINT",FACE,{"disambiguationData":[TD([[makeQuery(id+"F9.imprint","IMPRINT",EDGE,{"disambiguationData":[TD([[subQ2,1.0]])],"derivedFrom":subQ1}),-1.0]])]});}
            var Q25;
            {var subQ0=sQuery(id+"F9.wireOp",EDGE,"E35.bottom");var subQ1=sQuery(id+"F9.wireOp",EDGE,"E20.57.0.0");var subQ2=makeQuery(id+"F9.imprint","INTERSECT",VERTEX,{"derivedFrom":[subQ1,subQ0]});Q25=makeQuery(id+"F9.imprint","IMPRINT",FACE,{"disambiguationData":[TD([[makeQuery(id+"F9.imprint","IMPRINT",EDGE,{"disambiguationData":[TD([[subQ2,1.0]])],"derivedFrom":subQ1}),-1.0]])]});}
            var Q26;
            {var subQ0=sQuery(id+"F9.wireOp",EDGE,"E38.top");var subQ1=sQuery(id+"F9.wireOp",EDGE,"E20.56.0.0");var subQ2=makeQuery(id+"F9.imprint","INTERSECT",VERTEX,{"derivedFrom":[subQ1,subQ0]});Q26=makeQuery(id+"F9.imprint","IMPRINT",FACE,{"disambiguationData":[TD([[makeQuery(id+"F9.imprint","IMPRINT",EDGE,{"disambiguationData":[TD([[subQ2,-1.0]])],"derivedFrom":subQ1}),-1.0]])]});}
            var Q27;
            {var subQ0=sQuery(id+"F9.wireOp",EDGE,"E38.top");var subQ1=sQuery(id+"F9.wireOp",EDGE,"E20.58.0.0");var subQ2=makeQuery(id+"F9.imprint","INTERSECT",VERTEX,{"derivedFrom":[subQ1,subQ0]});Q27=makeQuery(id+"F9.imprint","IMPRINT",FACE,{"disambiguationData":[TD([[makeQuery(id+"F9.imprint","IMPRINT",EDGE,{"disambiguationData":[TD([[subQ2,-1.0]])],"derivedFrom":subQ1}),-1.0]])]});}
            var Q28;
            {var subQ0=sQuery(id+"F9.wireOp",EDGE,"E38.top");var subQ1=sQuery(id+"F9.wireOp",EDGE,"E20.60.0.0");var subQ2=makeQuery(id+"F9.imprint","INTERSECT",VERTEX,{"derivedFrom":[subQ1,subQ0]});Q28=makeQuery(id+"F9.imprint","IMPRINT",FACE,{"disambiguationData":[TD([[makeQuery(id+"F9.imprint","IMPRINT",EDGE,{"disambiguationData":[TD([[subQ2,-1.0]])],"derivedFrom":subQ1}),-1.0]])]});}
            var Q29;
            {var subQ3=sQuery(id+"F9.wireOp",EDGE,"E20.62.0.0");var subQ5=sQuery(id+"F9.wireOp",EDGE,"E38.top");var subQ6=makeQuery(id+"F9.imprint","INTERSECT",VERTEX,{"derivedFrom":[subQ3,subQ5]});Q29=makeQuery(id+"F9.imprint","IMPRINT",FACE,{"disambiguationData":[TD([[makeQuery(id+"F9.imprint","IMPRINT",EDGE,{"disambiguationData":[TD([[subQ6,-1.0]])],"derivedFrom":subQ3}),-1.0]])]});}
            var Q30;
            {var subQ0=sQuery(id+"F9.wireOp",EDGE,"E39.right");var subQ1=sQuery(id+"F9.wireOp",EDGE,"E20.64.0.0");var subQ2=makeQuery(id+"F9.imprint","INTERSECT",VERTEX,{"derivedFrom":[subQ1,subQ0]});Q30=makeQuery(id+"F9.imprint","IMPRINT",FACE,{"disambiguationData":[TD([[makeQuery(id+"F9.imprint","IMPRINT",EDGE,{"disambiguationData":[TD([[subQ2,1.0]])],"derivedFrom":subQ1}),-1.0]])]});}
            var Q31;
            {var subQ0=sQuery(id+"F9.wireOp",EDGE,"E39.right");var subQ1=sQuery(id+"F9.wireOp",EDGE,"E20.66.0.0");var subQ2=makeQuery(id+"F9.imprint","INTERSECT",VERTEX,{"derivedFrom":[subQ1,subQ0]});Q31=makeQuery(id+"F9.imprint","IMPRINT",FACE,{"disambiguationData":[TD([[makeQuery(id+"F9.imprint","IMPRINT",EDGE,{"disambiguationData":[TD([[subQ2,1.0]])],"derivedFrom":subQ1}),-1.0]])]});}
            var Q32;
            {var subQ0=sQuery(id+"F9.wireOp",EDGE,"E39.right");var subQ1=sQuery(id+"F9.wireOp",EDGE,"E20.68.0.0");var subQ2=makeQuery(id+"F9.imprint","INTERSECT",VERTEX,{"derivedFrom":[subQ1,subQ0]});Q32=makeQuery(id+"F9.imprint","IMPRINT",FACE,{"disambiguationData":[TD([[makeQuery(id+"F9.imprint","IMPRINT",EDGE,{"disambiguationData":[TD([[subQ2,1.0]])],"derivedFrom":subQ1}),-1.0]])]});}
            var Q33;
            {var subQ9=sQuery(id+"F9.wireOp",EDGE,"E20.70.0.0");var subQ12=sQuery(id+"F9.wireOp",EDGE,"E39.right");var subQ13=makeQuery(id+"F9.imprint","INTERSECT",VERTEX,{"derivedFrom":[subQ9,subQ12]});Q33=makeQuery(id+"F9.imprint","IMPRINT",FACE,{"disambiguationData":[TD([[makeQuery(id+"F9.imprint","IMPRINT",EDGE,{"disambiguationData":[TD([[subQ13,1.0]])],"derivedFrom":subQ9}),-1.0]])]});}
            var Q34;
            {var subQ0=sQuery(id+"F9.wireOp",EDGE,"E39.top");var subQ1=sQuery(id+"F9.wireOp",EDGE,"E20.74.0.0");var subQ2=makeQuery(id+"F9.imprint","INTERSECT",VERTEX,{"derivedFrom":[subQ1,subQ0]});Q34=makeQuery(id+"F9.imprint","IMPRINT",FACE,{"disambiguationData":[TD([[makeQuery(id+"F9.imprint","IMPRINT",EDGE,{"disambiguationData":[TD([[subQ2,1.0]])],"derivedFrom":subQ1}),-1.0]])]});}
            var Q35;
            {var subQ0=sQuery(id+"F9.wireOp",EDGE,"E39.top");var subQ1=sQuery(id+"F9.wireOp",EDGE,"E20.72.0.0");var subQ2=makeQuery(id+"F9.imprint","INTERSECT",VERTEX,{"derivedFrom":[subQ1,subQ0]});Q35=makeQuery(id+"F9.imprint","IMPRINT",FACE,{"disambiguationData":[TD([[makeQuery(id+"F9.imprint","IMPRINT",EDGE,{"disambiguationData":[TD([[subQ2,1.0]])],"derivedFrom":subQ1}),-1.0]])]});}
            var Q36;
            {var subQ0=sQuery(id+"F9.wireOp",EDGE,"E42.bottom");var subQ1=sQuery(id+"F9.wireOp",EDGE,"E20.72.0.0");var subQ2=makeQuery(id+"F9.imprint","INTERSECT",VERTEX,{"derivedFrom":[subQ1,subQ0]});Q36=makeQuery(id+"F9.imprint","IMPRINT",FACE,{"disambiguationData":[TD([[makeQuery(id+"F9.imprint","IMPRINT",EDGE,{"disambiguationData":[TD([[subQ2,-1.0]])],"derivedFrom":subQ1}),-1.0]])]});}
            var Q37;
            {var subQ0=sQuery(id+"F9.wireOp",EDGE,"E42.bottom");var subQ1=sQuery(id+"F9.wireOp",EDGE,"E20.74.0.0");var subQ2=makeQuery(id+"F9.imprint","INTERSECT",VERTEX,{"derivedFrom":[subQ1,subQ0]});Q37=makeQuery(id+"F9.imprint","IMPRINT",FACE,{"disambiguationData":[TD([[makeQuery(id+"F9.imprint","IMPRINT",EDGE,{"disambiguationData":[TD([[subQ2,-1.0]])],"derivedFrom":subQ1}),-1.0]])]});}
            var Q38;
            {var subQ0=sQuery(id+"F9.wireOp",EDGE,"E42.bottom");var subQ1=sQuery(id+"F9.wireOp",EDGE,"E20.76.0.0");var subQ2=makeQuery(id+"F9.imprint","INTERSECT",VERTEX,{"derivedFrom":[subQ1,subQ0]});Q38=makeQuery(id+"F9.imprint","IMPRINT",FACE,{"disambiguationData":[TD([[makeQuery(id+"F9.imprint","IMPRINT",EDGE,{"disambiguationData":[TD([[subQ2,-1.0]])],"derivedFrom":subQ1}),-1.0]])]});}
            var Q39;
            {var subQ0=sQuery(id+"F9.wireOp",EDGE,"E42.bottom");var subQ1=sQuery(id+"F9.wireOp",EDGE,"E20.78.0.0");var subQ2=makeQuery(id+"F9.imprint","INTERSECT",VERTEX,{"derivedFrom":[subQ1,subQ0]});Q39=makeQuery(id+"F9.imprint","IMPRINT",FACE,{"disambiguationData":[TD([[makeQuery(id+"F9.imprint","IMPRINT",EDGE,{"disambiguationData":[TD([[subQ2,-1.0]])],"derivedFrom":subQ1}),-1.0]])]});}
            var Q40;
            {var subQ0=sQuery(id+"F9.wireOp",EDGE,"E42.bottom");var subQ1=sQuery(id+"F9.wireOp",EDGE,"E20.80.0.0");var subQ2=makeQuery(id+"F9.imprint","INTERSECT",VERTEX,{"derivedFrom":[subQ1,subQ0]});Q40=makeQuery(id+"F9.imprint","IMPRINT",FACE,{"disambiguationData":[TD([[makeQuery(id+"F9.imprint","IMPRINT",EDGE,{"disambiguationData":[TD([[subQ2,-1.0]])],"derivedFrom":subQ1}),-1.0]])]});}
            var Q41;
            {var subQ0=sQuery(id+"F9.wireOp",EDGE,"E42.bottom");var subQ1=sQuery(id+"F9.wireOp",EDGE,"E20.82.0.0");var subQ2=makeQuery(id+"F9.imprint","INTERSECT",VERTEX,{"derivedFrom":[subQ1,subQ0]});Q41=makeQuery(id+"F9.imprint","IMPRINT",FACE,{"disambiguationData":[TD([[makeQuery(id+"F9.imprint","IMPRINT",EDGE,{"disambiguationData":[TD([[subQ2,-1.0]])],"derivedFrom":subQ1}),-1.0]])]});}
            var Q42;
            {var subQ0=sQuery(id+"F9.wireOp",EDGE,"E42.bottom");var subQ1=sQuery(id+"F9.wireOp",EDGE,"E20.84.0.0");var subQ2=makeQuery(id+"F9.imprint","INTERSECT",VERTEX,{"derivedFrom":[subQ1,subQ0]});Q42=makeQuery(id+"F9.imprint","IMPRINT",FACE,{"disambiguationData":[TD([[makeQuery(id+"F9.imprint","IMPRINT",EDGE,{"disambiguationData":[TD([[subQ2,-1.0]])],"derivedFrom":subQ1}),-1.0]])]});}
            var Q43;
            {var subQ0=sQuery(id+"F9.wireOp",EDGE,"E42.bottom");var subQ1=sQuery(id+"F9.wireOp",EDGE,"E20.86.0.0");var subQ2=makeQuery(id+"F9.imprint","INTERSECT",VERTEX,{"derivedFrom":[subQ1,subQ0]});Q43=makeQuery(id+"F9.imprint","IMPRINT",FACE,{"disambiguationData":[TD([[makeQuery(id+"F9.imprint","IMPRINT",EDGE,{"disambiguationData":[TD([[subQ2,-1.0]])],"derivedFrom":subQ1}),-1.0]])]});}
            var Q44;
            {var subQ0=sQuery(id+"F9.wireOp",EDGE,"E41.bottom");var subQ1=sQuery(id+"F9.wireOp",EDGE,"E20.88.0.0");var subQ2=makeQuery(id+"F9.imprint","INTERSECT",VERTEX,{"derivedFrom":[subQ1,subQ0]});Q44=makeQuery(id+"F9.imprint","IMPRINT",FACE,{"disambiguationData":[TD([[makeQuery(id+"F9.imprint","IMPRINT",EDGE,{"disambiguationData":[TD([[subQ2,1.0]])],"derivedFrom":subQ1}),-1.0]])]});}
            var Q45;
            {var subQ0=sQuery(id+"F9.wireOp",EDGE,"E41.bottom");var subQ1=sQuery(id+"F9.wireOp",EDGE,"E20.90.0.0");var subQ2=makeQuery(id+"F9.imprint","INTERSECT",VERTEX,{"derivedFrom":[subQ1,subQ0]});Q45=makeQuery(id+"F9.imprint","IMPRINT",FACE,{"disambiguationData":[TD([[makeQuery(id+"F9.imprint","IMPRINT",EDGE,{"disambiguationData":[TD([[subQ2,1.0]])],"derivedFrom":subQ1}),-1.0]])]});}
            var Q46;
            {var subQ0=sQuery(id+"F9.wireOp",EDGE,"E41.bottom");var subQ1=sQuery(id+"F9.wireOp",EDGE,"E20.92.0.0");var subQ2=makeQuery(id+"F9.imprint","INTERSECT",VERTEX,{"derivedFrom":[subQ1,subQ0]});Q46=makeQuery(id+"F9.imprint","IMPRINT",FACE,{"disambiguationData":[TD([[makeQuery(id+"F9.imprint","IMPRINT",EDGE,{"disambiguationData":[TD([[subQ2,1.0]])],"derivedFrom":subQ1}),-1.0]])]});}
            var Q47;
            {var subQ0=sQuery(id+"F9.wireOp",EDGE,"E25.left");var subQ1=sQuery(id+"F9.wireOp",EDGE,"E20.27.0.0");var subQ2=makeQuery(id+"F9.imprint","INTERSECT",VERTEX,{"derivedFrom":[subQ1,subQ0]});Q47=makeQuery(id+"F9.imprint","IMPRINT",FACE,{"disambiguationData":[TD([[makeQuery(id+"F9.imprint","IMPRINT",EDGE,{"disambiguationData":[TD([[subQ2,-1.0]])],"derivedFrom":subQ1}),-1.0]])]});}
            var Q48;
            {var subQ0=sQuery(id+"F9.wireOp",EDGE,"E39.top");var subQ1=sQuery(id+"F9.wireOp",EDGE,"E20.76.0.0");var subQ2=makeQuery(id+"F9.imprint","INTERSECT",VERTEX,{"derivedFrom":[subQ1,subQ0]});Q48=makeQuery(id+"F9.imprint","IMPRINT",FACE,{"disambiguationData":[TD([[makeQuery(id+"F9.imprint","IMPRINT",EDGE,{"disambiguationData":[TD([[subQ2,1.0]])],"derivedFrom":subQ1}),-1.0]])]});}
            var Q49;
            {var subQ0=sQuery(id+"F9.wireOp",EDGE,"E39.top");var subQ1=sQuery(id+"F9.wireOp",EDGE,"E20.78.0.0");var subQ2=makeQuery(id+"F9.imprint","INTERSECT",VERTEX,{"derivedFrom":[subQ1,subQ0]});Q49=makeQuery(id+"F9.imprint","IMPRINT",FACE,{"disambiguationData":[TD([[makeQuery(id+"F9.imprint","IMPRINT",EDGE,{"disambiguationData":[TD([[subQ2,1.0]])],"derivedFrom":subQ1}),-1.0]])]});}
            var Q50;
            {var subQ0=sQuery(id+"F9.wireOp",EDGE,"E41.bottom");var subQ1=sQuery(id+"F9.wireOp",EDGE,"E20.94.0.0");var subQ2=makeQuery(id+"F9.imprint","INTERSECT",VERTEX,{"derivedFrom":[subQ1,subQ0]});Q50=makeQuery(id+"F9.imprint","IMPRINT",FACE,{"disambiguationData":[TD([[makeQuery(id+"F9.imprint","IMPRINT",EDGE,{"disambiguationData":[TD([[subQ2,1.0]])],"derivedFrom":subQ1}),-1.0]])]});}
            var Q51;
            {var subQ0=sQuery(id+"F9.wireOp",EDGE,"E41.bottom");var subQ1=sQuery(id+"F9.wireOp",EDGE,"E20.96.0.0");var subQ2=makeQuery(id+"F9.imprint","INTERSECT",VERTEX,{"derivedFrom":[subQ1,subQ0]});Q51=makeQuery(id+"F9.imprint","IMPRINT",FACE,{"disambiguationData":[TD([[makeQuery(id+"F9.imprint","IMPRINT",EDGE,{"disambiguationData":[TD([[subQ2,1.0]])],"derivedFrom":subQ1}),-1.0]])]});}
            var Q52;
            {var subQ0=sQuery(id+"F9.wireOp",EDGE,"E41.bottom");var subQ1=sQuery(id+"F9.wireOp",EDGE,"E20.98.0.0");var subQ2=makeQuery(id+"F9.imprint","INTERSECT",VERTEX,{"derivedFrom":[subQ1,subQ0]});Q52=makeQuery(id+"F9.imprint","IMPRINT",FACE,{"disambiguationData":[TD([[makeQuery(id+"F9.imprint","IMPRINT",EDGE,{"disambiguationData":[TD([[subQ2,1.0]])],"derivedFrom":subQ1}),-1.0]])]});}
            var Q53;
            {var subQ0=sQuery(id+"F9.wireOp",EDGE,"E41.bottom");var subQ1=sQuery(id+"F9.wireOp",EDGE,"E40.1.0.0");var subQ2=makeQuery(id+"F9.imprint","INTERSECT",VERTEX,{"derivedFrom":[subQ1,subQ0]});Q53=makeQuery(id+"F9.imprint","IMPRINT",FACE,{"disambiguationData":[TD([[makeQuery(id+"F9.imprint","IMPRINT",EDGE,{"disambiguationData":[TD([[subQ2,1.0]])],"derivedFrom":subQ1}),-1.0]])]});}
            var Q54;
            {var subQ0=sQuery(id+"F9.wireOp",EDGE,"E33.top");var subQ1=sQuery(id+"F9.wireOp",EDGE,"E20.11.0.0");var subQ2=makeQuery(id+"F9.imprint","INTERSECT",VERTEX,{"derivedFrom":[subQ1,subQ0]});Q54=makeQuery(id+"F9.imprint","IMPRINT",FACE,{"disambiguationData":[TD([[makeQuery(id+"F9.imprint","IMPRINT",EDGE,{"disambiguationData":[TD([[subQ2,-1.0]])],"derivedFrom":subQ1}),-1.0]])]});}
            var Q55;
            {var subQ0=sQuery(id+"F9.wireOp",EDGE,"E41.bottom");var subQ1=sQuery(id+"F9.wireOp",EDGE,"E40.3.0.0");var subQ2=makeQuery(id+"F9.imprint","INTERSECT",VERTEX,{"derivedFrom":[subQ1,subQ0]});Q55=makeQuery(id+"F9.imprint","IMPRINT",FACE,{"disambiguationData":[TD([[makeQuery(id+"F9.imprint","IMPRINT",EDGE,{"disambiguationData":[TD([[subQ2,1.0]])],"derivedFrom":subQ1}),-1.0]])]});}
            var Q56;
            Q56=sQuery(id+"F10.wireOp",VERTEX,"E46.end");
            extrude(context, id + "F11", {"entities" : qUnion([Q0, Q1, Q2, Q3, Q4, Q5, Q6, Q7, Q8, Q9, Q10, Q11, Q12, Q13, Q14, Q15, Q16, Q17, Q18, Q19, Q20, Q21, Q22, Q23, Q24, Q25, Q26, Q27, Q28, Q29, Q30, Q31, Q32, Q33, Q34, Q35, Q36, Q37, Q38, Q39, Q40, Q41, Q42, Q43, Q44, Q45, Q46, Q47, Q48, Q49, Q50, Q51, Q52, Q53, Q54, Q55]), "operationType" : NewBodyOperationType.REMOVE, "endBound" : BoundingType.UP_TO_VERTEX, "oppositeDirection" : true, "endBoundEntityVertex" : qUnion([Q56]), "depth" : 1 * mm});
        }
        {
            var Q0;
            Q0=makeQuery(id+"F11.boolean.opBoolean","SPLIT",BODY,{"disambiguationData":[OD(1.0)],"derivedFrom":makeQuery(id+"F1.opExtrude","SWEPT_BODY",BODY,{"disambiguationData":[OSD([sQuery(id+"F0.wireOp",EDGE,"E0.bottom"),sQuery(id+"F0.wireOp",EDGE,"E0.top"),sQuery(id+"F0.wireOp",EDGE,"E0.left"),sQuery(id+"F0.wireOp",EDGE,"E0.right"),sQuery(id+"F0.wireOp",EDGE,"E1"),sQuery(id+"F0.wireOp",EDGE,"E7"),sQuery(id+"F0.wireOp",EDGE,"E8")])]})});
            var Q1;
            Q1=qCreatedBy(makeId("Right.planeOp"),FACE);
            mirror(context, id + "F12", {"entities" : qUnion([Q0]), "mirrorPlane" : qUnion([Q1])});
        }
    });
